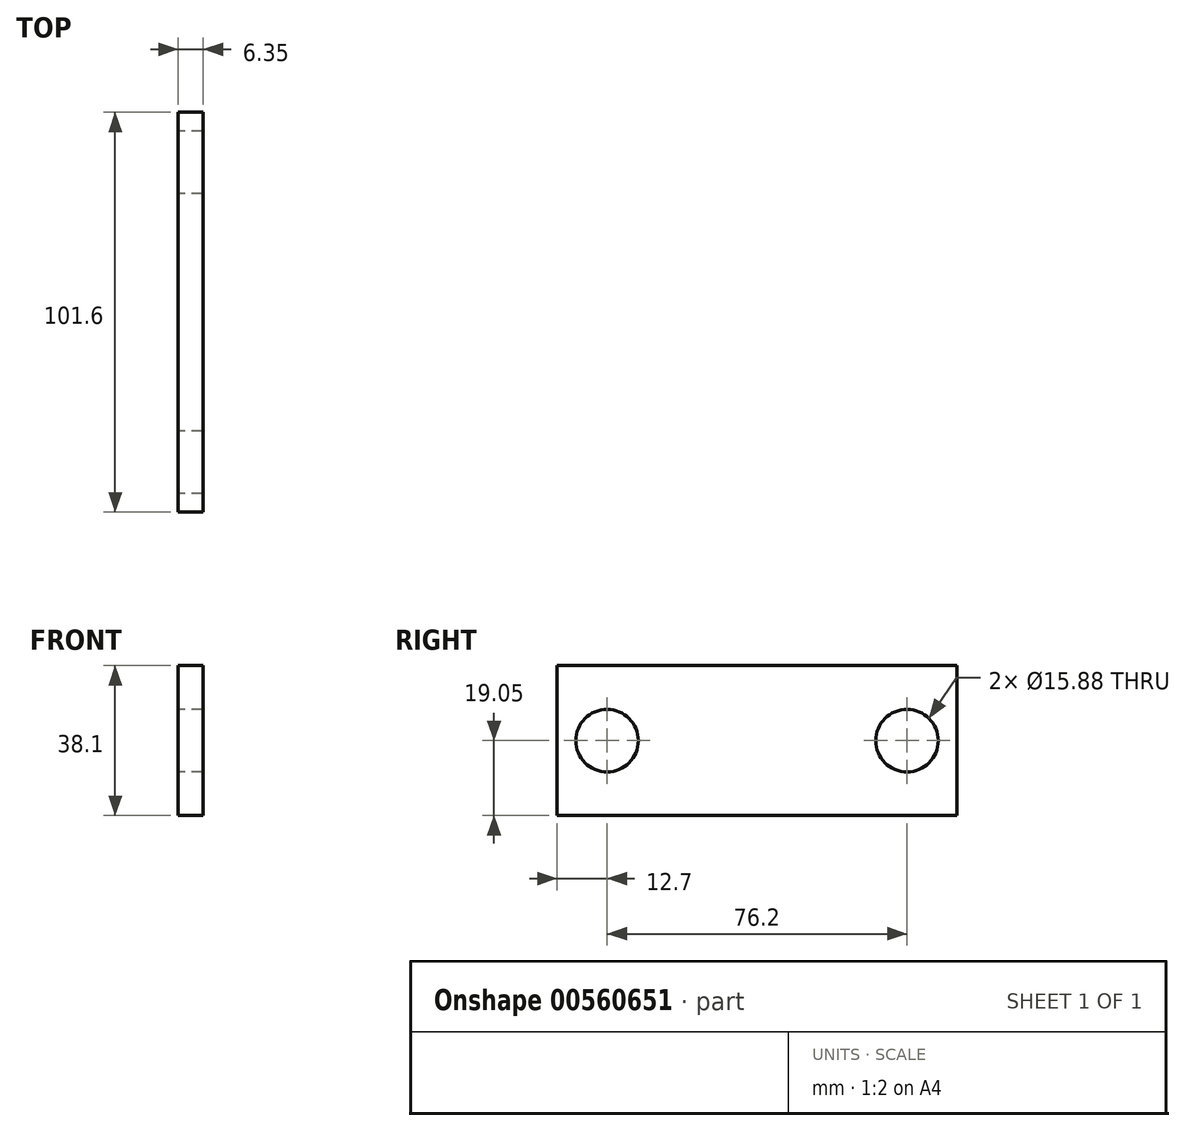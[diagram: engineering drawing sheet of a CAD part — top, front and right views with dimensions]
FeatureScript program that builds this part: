
annotation { "Feature Type Name" : "Feature", "Feature Type Description" : "" }
export const myFeature = defineFeature(function(context is Context, id is Id, definition is map)
    precondition{}
    {
        {
            var Q0;
            Q0=qCreatedBy(makeId("Right.planeOp"),FACE);
            var sketch = newSketch(context, id + "F0", { "sketchPlane" : qUnion([Q0])});
            skLineSegment(sketch, "E0.bottom", {"start": v(0, 0) * mm, "end": v(101.6, 0) * mm});
            skLineSegment(sketch, "E0.top", {"start": v(0, -38.1) * mm, "end": v(101.6, -38.1) * mm});
            skLineSegment(sketch, "E0.left", {"start": v(0, 0) * mm, "end": v(0, -38.1) * mm});
            skLineSegment(sketch, "E0.right", {"start": v(101.6, 0) * mm, "end": v(101.6, -38.1) * mm});
            skCircle(sketch, "E1", {"center": v(12.7, -19.05) * mm, "radius": 7.94 * mm});
            skCircle(sketch, "E2", {"center": v(88.9, -19.05) * mm, "radius": 7.94 * mm});
            skSolve(sketch);
        }
        {
            var Q0;
            Q0 = qSketchRegion(id + "F0", true);
            extrude(context, id + "F1", {"entities" : qUnion([Q0]), "depth" : 6.35 * mm, "offsetDistance" : 25.4 * mm});
        }
    });
